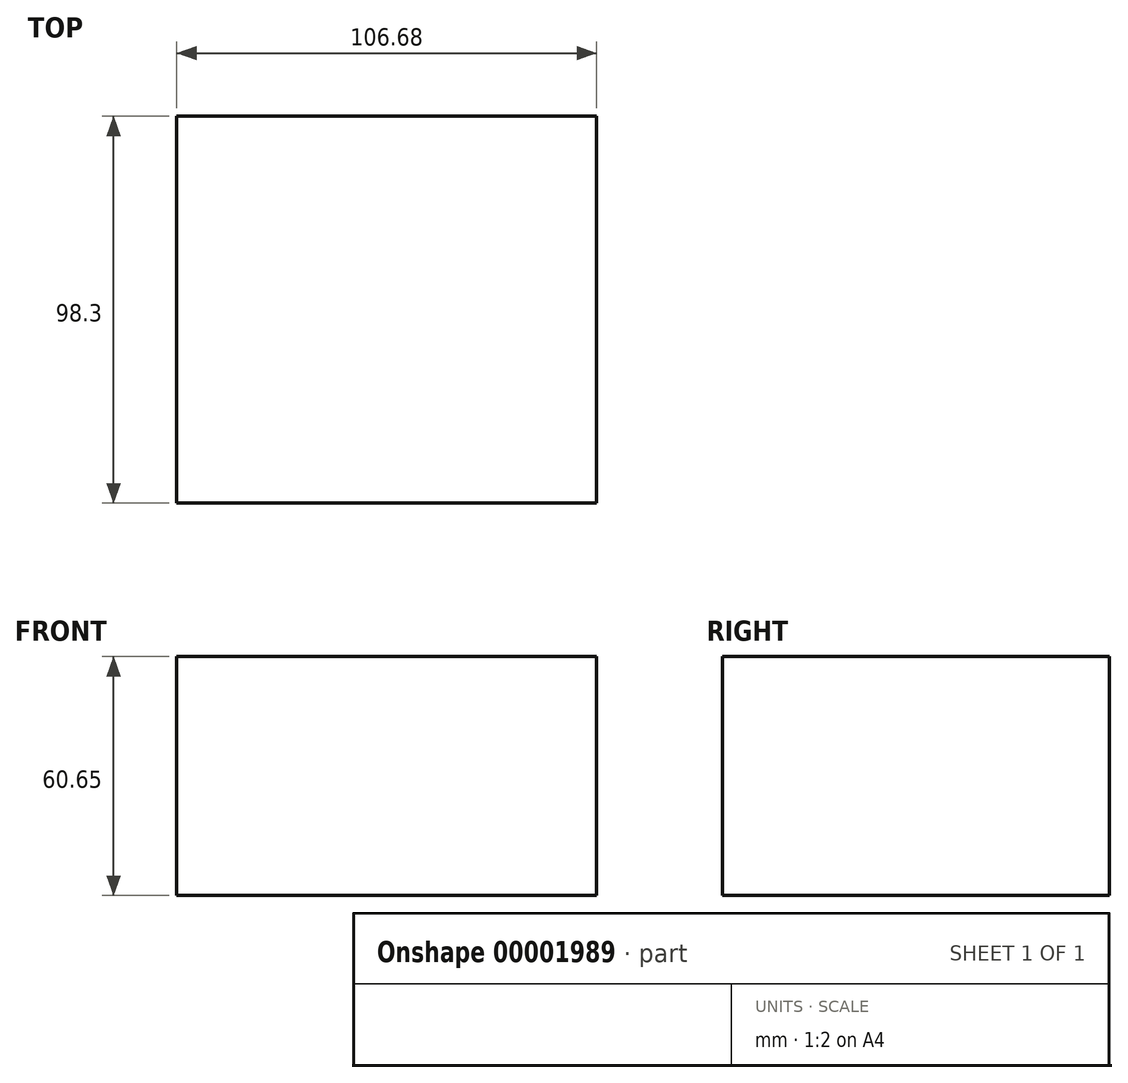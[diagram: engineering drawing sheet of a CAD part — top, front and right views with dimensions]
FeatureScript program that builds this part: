
annotation { "Feature Type Name" : "Feature", "Feature Type Description" : "" }
export const myFeature = defineFeature(function(context is Context, id is Id, definition is map)
    precondition{}
    {
        {
            var Q0;
            Q0=qCreatedBy(makeId("Top.planeOp"),FACE);
            var sketch = newSketch(context, id + "F0", { "sketchPlane" : qUnion([Q0])});
            skLineSegment(sketch, "E0.bottom", {"start": v(0, 0) * mm, "end": v(106.68, 0) * mm});
            skLineSegment(sketch, "E0.top", {"start": v(0, 98.3) * mm, "end": v(106.68, 98.3) * mm});
            skLineSegment(sketch, "E0.left", {"start": v(0, 0) * mm, "end": v(0, 98.3) * mm});
            skLineSegment(sketch, "E0.right", {"start": v(106.68, 0) * mm, "end": v(106.68, 98.3) * mm});
            skSolve(sketch);
        }
        {
            var Q0;
            Q0=makeQuery(id+"F0.imprint","IMPRINT",FACE,{"disambiguationData":[TD([[makeQuery(id+"F0.imprint","IMPRINT",EDGE,{"derivedFrom":sQuery(id+"F0.wireOp",EDGE,"E0.bottom")}),1.0]])]});
            extrude(context, id + "F1", {"entities" : qUnion([Q0]), "depth" : 60.65 * mm});
        }
    });
